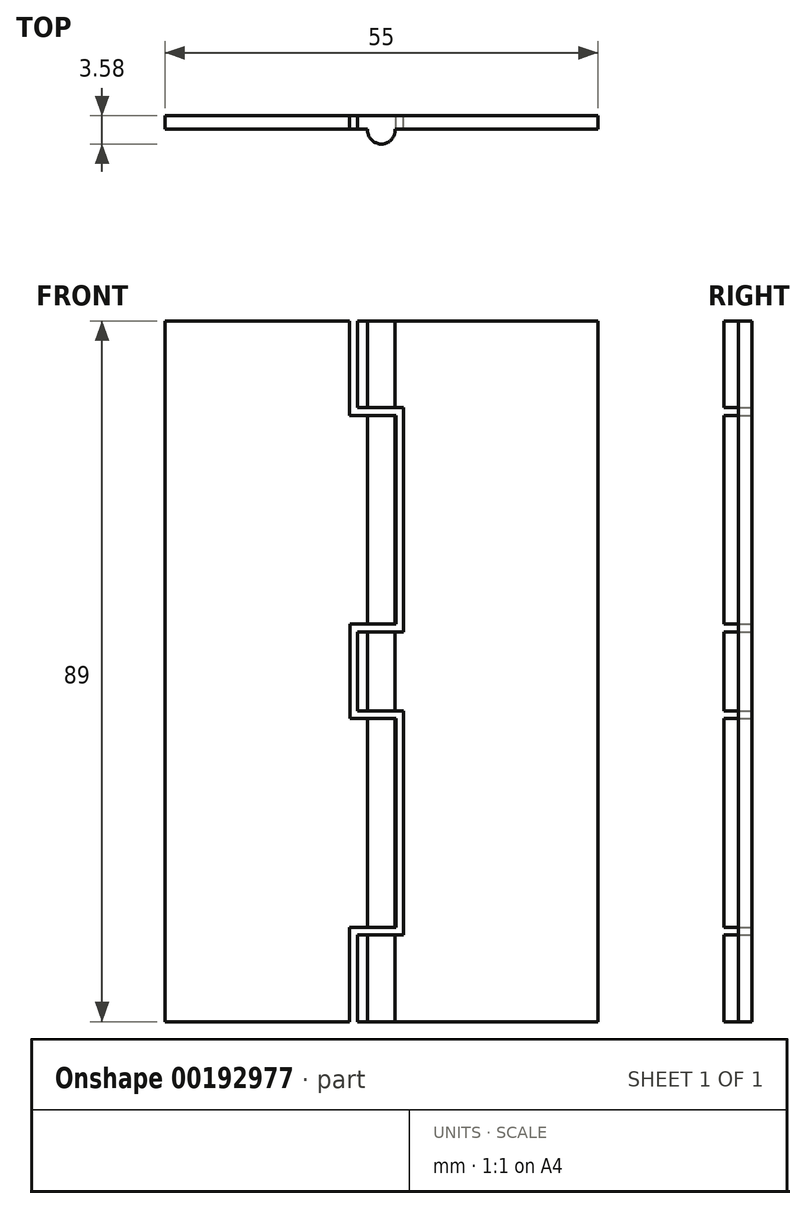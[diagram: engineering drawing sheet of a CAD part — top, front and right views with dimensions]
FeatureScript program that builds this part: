
annotation { "Feature Type Name" : "Feature", "Feature Type Description" : "" }
export const myFeature = defineFeature(function(context is Context, id is Id, definition is map)
    precondition{}
    {
        {
            var Q0;
            Q0=qCreatedBy(makeId("Front.planeOp"),FACE);
            var sketch = newSketch(context, id + "F0", { "sketchPlane" : qUnion([Q0])});
            skLineSegment(sketch, "E0.bottom", {"start": v(27.5, 0) * mm, "end": v(-27.5, 0) * mm});
            skLineSegment(sketch, "E0.top", {"start": v(27.5, 89) * mm, "end": v(-27.5, 89) * mm});
            skLineSegment(sketch, "E0.left", {"start": v(27.5, 0) * mm, "end": v(27.5, 89) * mm});
            skLineSegment(sketch, "E0.right", {"start": v(-27.5, 0) * mm, "end": v(-27.5, 89) * mm});
            skSolve(sketch);
        }
        {
            var Q0;
            Q0=makeQuery(id+"F0.imprint","IMPRINT",FACE,{"disambiguationData":[TD([[makeQuery(id+"F0.imprint","IMPRINT",EDGE,{"derivedFrom":sQuery(id+"F0.wireOp",EDGE,"E0.bottom")}),-1.0]])]});
            extrude(context, id + "F1", {"entities" : qUnion([Q0]), "depth" : 1.7 * mm});
        }
        {
            var Q0;
            Q0=qCreatedBy(makeId("Top.planeOp"),FACE);
            var sketch = newSketch(context, id + "F2", { "sketchPlane" : qUnion([Q0])});
            skCircle(sketch, "E1", {"center": v(0, -1.83) * mm, "radius": 1.75 * mm});
            skSolve(sketch);
        }
        {
            var Q0;
            Q0 = qSketchRegion(id + "F2", true);
            var Q1;
            Q1=makeQuery(id+"F1.opExtrude","SWEPT_FACE",FACE,{"disambiguationData":[OSD([sQuery(id+"F0.wireOp",EDGE,"E0.top")])]});
            extrude(context, id + "F3", {"entities" : qUnion([Q0]), "operationType" : NewBodyOperationType.ADD, "endBound" : BoundingType.UP_TO_SURFACE, "endBoundEntityFace" : qUnion([Q1]), "depth" : 25 * mm});
        }
        {
            var Q0;
            Q0=qCreatedBy(makeId("Front.planeOp"),FACE);
            var sketch = newSketch(context, id + "F4", { "sketchPlane" : qUnion([Q0])});
            skLineSegment(sketch, "E2.bottom", {"start": v(-4.06, 89) * mm, "end": v(-3.06, 89) * mm});
            skLineSegment(sketch, "E2.left", {"start": v(-4.06, 89) * mm, "end": v(-4.06, 77) * mm});
            skLineSegment(sketch, "E2.right", {"start": v(-3.06, 89) * mm, "end": v(-3.06, 78) * mm});
            skLineSegment(sketch, "E3", {"start": v(-27.5, 44.5) * mm, "end": v(27.5, 44.5) * mm, "construction": true});
            skLineSegment(sketch, "E4", {"start": v(-3.06, 78) * mm, "end": v(2.83, 78) * mm});
            skLineSegment(sketch, "E5", {"start": v(2.83, 78) * mm, "end": v(2.83, 49.5) * mm});
            skLineSegment(sketch, "E6", {"start": v(2.83, 49.5) * mm, "end": v(-3.06, 49.5) * mm});
            skLineSegment(sketch, "E7", {"start": v(-4.06, 77) * mm, "end": v(1.83, 77) * mm});
            skLineSegment(sketch, "E8", {"start": v(1.83, 77) * mm, "end": v(1.83, 50.5) * mm});
            skLineSegment(sketch, "E9", {"start": v(1.83, 50.5) * mm, "end": v(-3.97, 50.5) * mm});
            skPoint(sketch, "E10.endSnap0", {"position": v(0, 44.5) * mm});
            skLineSegment(sketch, "E11", {"start": v(1.83, 63.75) * mm, "end": v(2.83, 63.75) * mm, "construction": true});
            skLineSegment(sketch, "E12", {"start": v(-0.12, 50.5) * mm, "end": v(-0.12, 49.5) * mm, "construction": true});
            skPoint(sketch, "E12.startSnap0", {"position": v(-0.12, 49.5) * mm});
            skLineSegment(sketch, "E13", {"start": v(-4.06, 83) * mm, "end": v(-3.06, 83) * mm, "construction": true});
            skLineSegment(sketch, "E14.MirrorCS", {"start": v(-4.06, 0) * mm, "end": v(-3.06, 0) * mm});
            skLineSegment(sketch, "E15.MirrorCS", {"start": v(-0.12, 38.5) * mm, "end": v(-0.12, 39.5) * mm, "construction": true});
            skLineSegment(sketch, "E16.MirrorCS", {"start": v(1.83, 38.5) * mm, "end": v(-3.97, 38.5) * mm});
            skLineSegment(sketch, "E17.MirrorCS", {"start": v(1.83, 25.25) * mm, "end": v(2.83, 25.25) * mm, "construction": true});
            skLineSegment(sketch, "E18.MirrorCS", {"start": v(-4.06, 6) * mm, "end": v(-3.06, 6) * mm, "construction": true});
            skLineSegment(sketch, "E19.MirrorCS", {"start": v(2.83, 39.5) * mm, "end": v(-3.06, 39.5) * mm});
            skLineSegment(sketch, "E20.MirrorCS", {"start": v(-3.06, 0) * mm, "end": v(-3.06, 11) * mm});
            skLineSegment(sketch, "E21.MirrorCS", {"start": v(2.83, 11) * mm, "end": v(2.83, 39.5) * mm});
            skLineSegment(sketch, "E22.MirrorCS", {"start": v(-4.06, 0) * mm, "end": v(-4.06, 12) * mm});
            skLineSegment(sketch, "E23.MirrorCS", {"start": v(1.83, 12) * mm, "end": v(1.83, 38.5) * mm});
            skLineSegment(sketch, "E24.MirrorCS", {"start": v(-3.06, 11) * mm, "end": v(2.83, 11) * mm});
            skPoint(sketch, "E25.MirrorP", {"position": v(-0.12, 39.5) * mm});
            skLineSegment(sketch, "E26.MirrorCS", {"start": v(-4.06, 12) * mm, "end": v(1.83, 12) * mm});
            skLineSegment(sketch, "E27", {"start": v(-3.06, 39.5) * mm, "end": v(-3.06, 49.5) * mm});
            skLineSegment(sketch, "E28", {"start": v(-3.97, 50.5) * mm, "end": v(-3.97, 38.5) * mm});
            skSolve(sketch);
        }
        {
            var Q0;
            Q0 = qSketchRegion(id + "F4", true);
            extrude(context, id + "F5", {"entities" : qUnion([Q0]), "operationType" : NewBodyOperationType.REMOVE, "endBound" : BoundingType.THROUGH_ALL, "depth" : 25 * mm});
        }
    });
